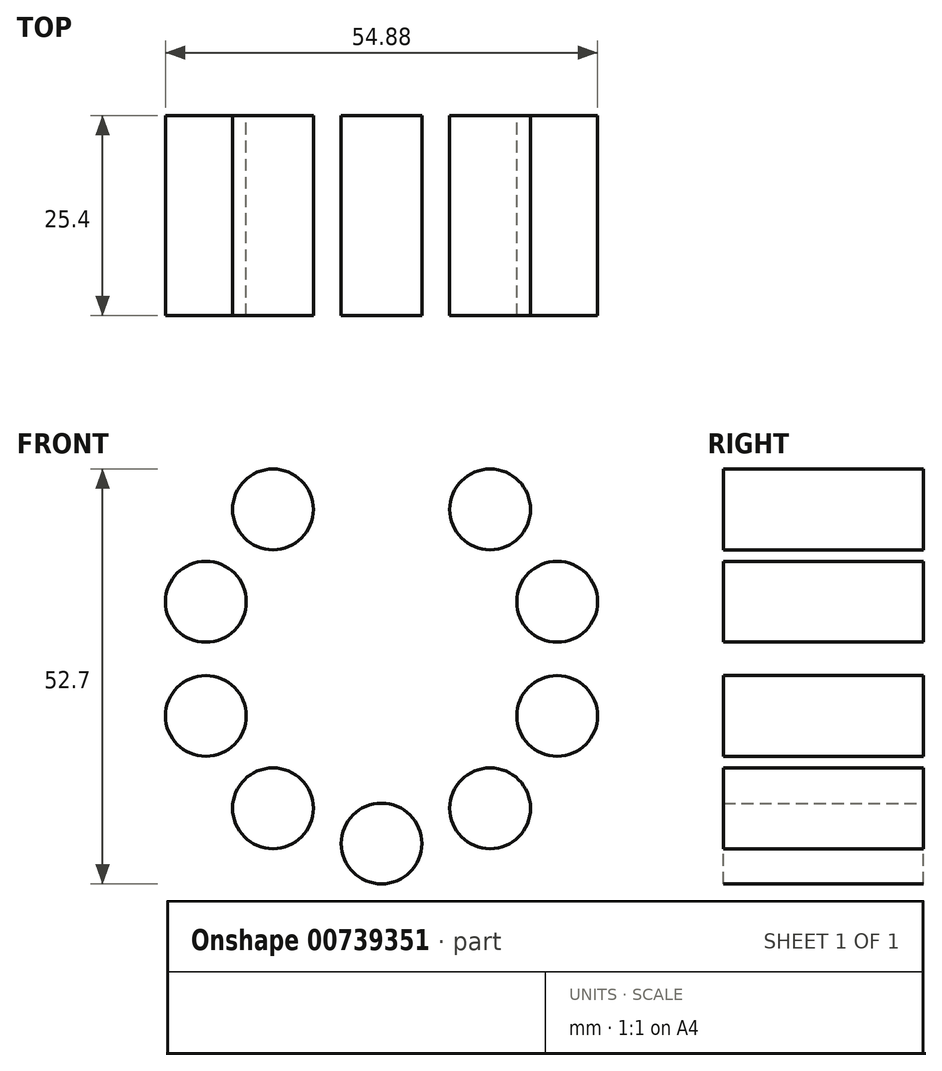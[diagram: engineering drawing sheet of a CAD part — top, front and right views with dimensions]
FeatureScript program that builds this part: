
annotation { "Feature Type Name" : "Feature", "Feature Type Description" : "" }
export const myFeature = defineFeature(function(context is Context, id is Id, definition is map)
    precondition{}
    {
        {
            var Q0;
            Q0=qCreatedBy(makeId("Front.planeOp"),FACE);
            var sketch = newSketch(context, id + "F0", { "sketchPlane" : qUnion([Q0])});
            skCircle(sketch, "E0", {"center": v(0, 23.46) * mm, "radius": 5.13 * mm});
            skCircle(sketch, "E1.1.0", {"center": v(13.8, 18.98) * mm, "radius": 5.13 * mm});
            skCircle(sketch, "E1.2.0", {"center": v(22.32, 7.25) * mm, "radius": 5.13 * mm});
            skCircle(sketch, "E1.3.0", {"center": v(22.32, -7.25) * mm, "radius": 5.13 * mm});
            skCircle(sketch, "E1.4.0", {"center": v(13.8, -18.98) * mm, "radius": 5.13 * mm});
            skCircle(sketch, "E1.5.0", {"center": v(0, -23.46) * mm, "radius": 5.13 * mm});
            skCircle(sketch, "E1.6.0", {"center": v(-13.8, -18.98) * mm, "radius": 5.13 * mm});
            skCircle(sketch, "E1.7.0", {"center": v(-22.32, -7.25) * mm, "radius": 5.13 * mm});
            skCircle(sketch, "E1.8.0", {"center": v(-22.32, 7.25) * mm, "radius": 5.13 * mm});
            skCircle(sketch, "E1.9.0", {"center": v(-13.8, 18.98) * mm, "radius": 5.13 * mm});
            skPoint(sketch, "E1.center", {"position": v(0, 0) * mm});
            skLineSegment(sketch, "E1.anchor1", {"start": v(0, 0) * mm, "end": v(0, 23.46) * mm, "construction": true});
            skLineSegment(sketch, "E1.anchor2", {"start": v(0, 0) * mm, "end": v(-13.8, 18.98) * mm, "construction": true});
            skSolve(sketch);
        }
        {
            var Q0;
            Q0=makeQuery(id+"F0.imprint","IMPRINT",FACE,{"disambiguationData":[TD([[makeQuery(id+"F0.imprint","IMPRINT",EDGE,{"derivedFrom":sQuery(id+"F0.wireOp",EDGE,"E0")}),1.0]])]});
            var sketch = newSketch(context, id + "F1", { "sketchPlane" : qUnion([Q0])});
            skSolve(sketch);
        }
        {
            var Q0;
            Q0=makeQuery(id+"F1.imprint","IMPRINT",FACE,{"disambiguationData":[TD([[makeQuery(id+"F1.imprint","IMPRINT",EDGE,{"derivedFrom":makeQuery(id+"F0.imprint","IMPRINT",EDGE,{"derivedFrom":sQuery(id+"F0.wireOp",EDGE,"E0")})}),1.0]])]});
            var Q1;
            Q1=makeQuery(id+"F0.imprint","IMPRINT",FACE,{"disambiguationData":[TD([[makeQuery(id+"F0.imprint","IMPRINT",EDGE,{"derivedFrom":sQuery(id+"F0.wireOp",EDGE,"E1.1.0")}),1.0]])]});
            var Q2;
            Q2=makeQuery(id+"F0.imprint","IMPRINT",FACE,{"disambiguationData":[TD([[makeQuery(id+"F0.imprint","IMPRINT",EDGE,{"derivedFrom":sQuery(id+"F0.wireOp",EDGE,"E1.2.0")}),1.0]])]});
            var Q3;
            Q3=makeQuery(id+"F0.imprint","IMPRINT",FACE,{"disambiguationData":[TD([[makeQuery(id+"F0.imprint","IMPRINT",EDGE,{"derivedFrom":sQuery(id+"F0.wireOp",EDGE,"E1.3.0")}),1.0]])]});
            var Q4;
            Q4=makeQuery(id+"F0.imprint","IMPRINT",FACE,{"disambiguationData":[TD([[makeQuery(id+"F0.imprint","IMPRINT",EDGE,{"derivedFrom":sQuery(id+"F0.wireOp",EDGE,"E1.4.0")}),1.0]])]});
            var Q5;
            Q5=makeQuery(id+"F0.imprint","IMPRINT",FACE,{"disambiguationData":[TD([[makeQuery(id+"F0.imprint","IMPRINT",EDGE,{"derivedFrom":sQuery(id+"F0.wireOp",EDGE,"E1.5.0")}),1.0]])]});
            var Q6;
            Q6=makeQuery(id+"F0.imprint","IMPRINT",FACE,{"disambiguationData":[TD([[makeQuery(id+"F0.imprint","IMPRINT",EDGE,{"derivedFrom":sQuery(id+"F0.wireOp",EDGE,"E1.6.0")}),1.0]])]});
            var Q7;
            Q7=makeQuery(id+"F0.imprint","IMPRINT",FACE,{"disambiguationData":[TD([[makeQuery(id+"F0.imprint","IMPRINT",EDGE,{"derivedFrom":sQuery(id+"F0.wireOp",EDGE,"E1.7.0")}),1.0]])]});
            var Q8;
            Q8=makeQuery(id+"F0.imprint","IMPRINT",FACE,{"disambiguationData":[TD([[makeQuery(id+"F0.imprint","IMPRINT",EDGE,{"derivedFrom":sQuery(id+"F0.wireOp",EDGE,"E1.8.0")}),1.0]])]});
            var Q9;
            Q9=makeQuery(id+"F0.imprint","IMPRINT",FACE,{"disambiguationData":[TD([[makeQuery(id+"F0.imprint","IMPRINT",EDGE,{"derivedFrom":sQuery(id+"F0.wireOp",EDGE,"E1.9.0")}),1.0]])]});
            extrude(context, id + "F2", {"entities" : qUnion([Q0, Q1, Q2, Q3, Q4, Q5, Q6, Q7, Q8, Q9]), "depth" : 25.4 * mm, "offsetDistance" : 25.4 * mm});
        }
    });
